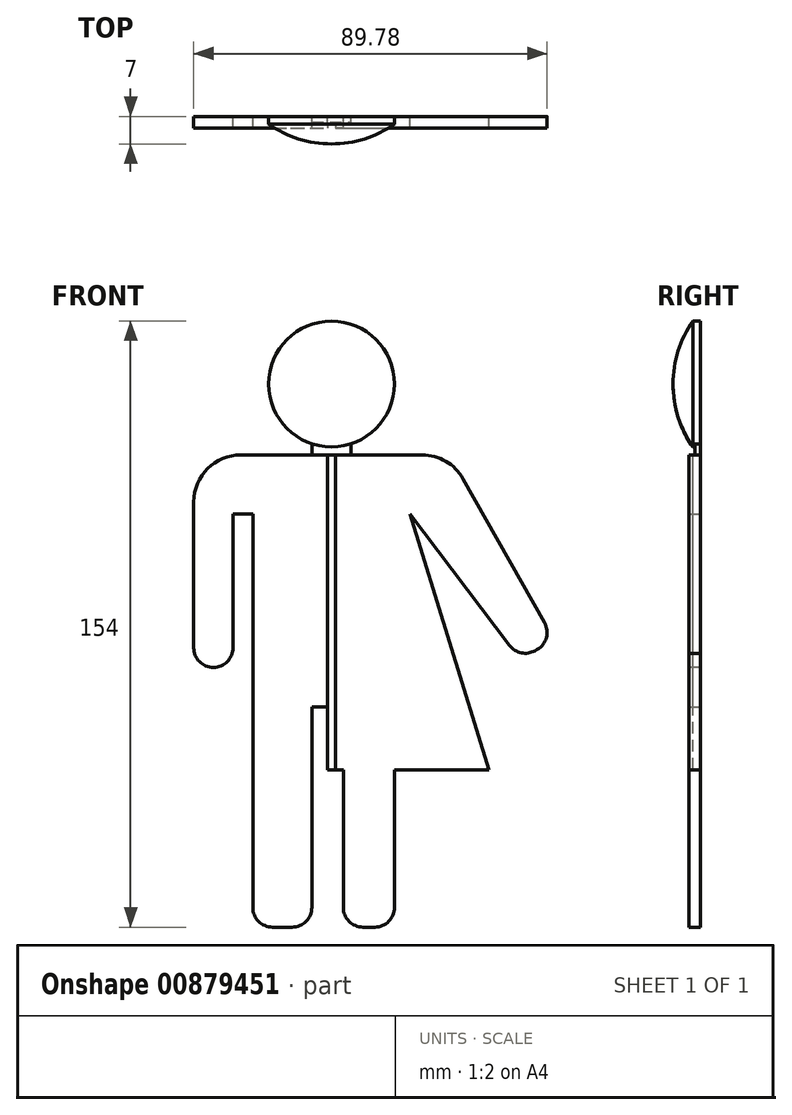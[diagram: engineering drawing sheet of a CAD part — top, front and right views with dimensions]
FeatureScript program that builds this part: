
annotation { "Feature Type Name" : "Feature", "Feature Type Description" : "" }
export const myFeature = defineFeature(function(context is Context, id is Id, definition is map)
    precondition{}
    {
        {
            var Q0;
            Q0=qCreatedBy(makeId("Front.planeOp"),FACE);
            var sketch = newSketch(context, id + "F0", { "sketchPlane" : qUnion([Q0])});
            skLineSegment(sketch, "E0.bottom", {"start": v(-60, 100) * mm, "end": v(60, 100) * mm});
            skLineSegment(sketch, "E0.top", {"start": v(-60, -100) * mm, "end": v(60, -100) * mm});
            skLineSegment(sketch, "E0.left", {"start": v(-60, 100) * mm, "end": v(-60, -100) * mm});
            skLineSegment(sketch, "E0.right", {"start": v(60, 100) * mm, "end": v(60, -100) * mm});
            skPoint(sketch, "E0.middle", {"position": v(0, 0) * mm});
            skCircle(sketch, "E1", {"center": v(0, 65) * mm, "radius": 15 * mm});
            skLineSegment(sketch, "E2.bottom", {"start": v(-20, 47) * mm, "end": v(20, 47) * mm});
            skLineSegment(sketch, "E2.top", {"start": v(-20, -73) * mm, "end": v(20, -73) * mm});
            skLineSegment(sketch, "E2.left", {"start": v(-20, 47) * mm, "end": v(-20, -73) * mm});
            skLineSegment(sketch, "E2.right", {"start": v(20, 47) * mm, "end": v(20, -73) * mm});
            skLineSegment(sketch, "E3.bottom", {"start": v(-20, 47) * mm, "end": v(-35, 47) * mm});
            skLineSegment(sketch, "E3.top", {"start": v(-20, -7) * mm, "end": v(-35, -7) * mm});
            skLineSegment(sketch, "E3.left", {"start": v(-20, 47) * mm, "end": v(-20, -7) * mm});
            skLineSegment(sketch, "E3.right", {"start": v(-35, 47) * mm, "end": v(-35, -7) * mm});
            skLineSegment(sketch, "E4.bottom", {"start": v(-5, -73) * mm, "end": v(3, -73) * mm});
            skLineSegment(sketch, "E4.top", {"start": v(-5, -17) * mm, "end": v(3, -17) * mm});
            skLineSegment(sketch, "E4.left", {"start": v(-5, -73) * mm, "end": v(-5, -17) * mm});
            skLineSegment(sketch, "E4.right", {"start": v(3, -73) * mm, "end": v(3, -17) * mm});
            skLineSegment(sketch, "E5.bottom", {"start": v(20, -73) * mm, "end": v(16, -73) * mm});
            skLineSegment(sketch, "E5.top", {"start": v(20, -33) * mm, "end": v(16, -33) * mm});
            skLineSegment(sketch, "E5.left", {"start": v(20, -73) * mm, "end": v(20, -33) * mm});
            skLineSegment(sketch, "E5.right", {"start": v(16, -73) * mm, "end": v(16, -33) * mm});
            skLineSegment(sketch, "E6", {"start": v(20, -33) * mm, "end": v(40, -33) * mm});
            skLineSegment(sketch, "E7", {"start": v(40, -33) * mm, "end": v(20, 32) * mm});
            skLineSegment(sketch, "E8", {"start": v(20, 47) * mm, "end": v(30, 47) * mm});
            skLineSegment(sketch, "E9", {"start": v(30, 47) * mm, "end": v(56.59, 0) * mm});
            skLineSegment(sketch, "E10", {"start": v(56.59, 0) * mm, "end": v(47.89, -4.92) * mm});
            skLineSegment(sketch, "E11", {"start": v(47.89, -4.92) * mm, "end": v(20, 32) * mm});
            skLineSegment(sketch, "E12.bottom", {"start": v(-20, -7) * mm, "end": v(-25, -7) * mm});
            skLineSegment(sketch, "E12.top", {"start": v(-20, 32) * mm, "end": v(-25, 32) * mm});
            skLineSegment(sketch, "E12.left", {"start": v(-20, -7) * mm, "end": v(-20, 32) * mm});
            skLineSegment(sketch, "E12.right", {"start": v(-25, -7) * mm, "end": v(-25, 32) * mm});
            skLineSegment(sketch, "E13.bottom", {"start": v(-5, 53) * mm, "end": v(5, 53) * mm});
            skLineSegment(sketch, "E13.top", {"start": v(-5, 41) * mm, "end": v(5, 41) * mm});
            skLineSegment(sketch, "E13.left", {"start": v(-5, 53) * mm, "end": v(-5, 41) * mm});
            skLineSegment(sketch, "E13.right", {"start": v(5, 53) * mm, "end": v(5, 41) * mm});
            skPoint(sketch, "E13.middle", {"position": v(0, 47) * mm});
            skLineSegment(sketch, "E14.bottom", {"start": v(16, -33) * mm, "end": v(-1, -33) * mm});
            skLineSegment(sketch, "E14.top", {"start": v(16, -17) * mm, "end": v(-1, -17) * mm});
            skLineSegment(sketch, "E14.left", {"start": v(16, -33) * mm, "end": v(16, -17) * mm});
            skLineSegment(sketch, "E14.right", {"start": v(-1, -33) * mm, "end": v(-1, -17) * mm});
            skSolve(sketch);
        }
        {
            var Q0;
            {var subQ5=sQuery(id+"F0.wireOp",EDGE,"E13.top");Q0=makeQuery(id+"F0.imprint","IMPRINT",FACE,{"disambiguationData":[TD([[makeQuery(id+"F0.imprint","IMPRINT",EDGE,{"derivedFrom":subQ5}),1.0]])]});}
            var Q1;
            {var subQ6=sQuery(id+"F0.wireOp",EDGE,"E2.left");Q1=makeQuery(id+"F0.imprint","IMPRINT",FACE,{"disambiguationData":[TD([[makeQuery(id+"F0.imprint","IMPRINT",EDGE,{"derivedFrom":subQ6}),1.0]])]});}
            var Q2;
            Q2=makeQuery(id+"F0.imprint","IMPRINT",FACE,{"disambiguationData":[TD([[makeQuery(id+"F0.imprint","IMPRINT",EDGE,{"derivedFrom":sQuery(id+"F0.wireOp",EDGE,"E3.bottom")}),1.0]])]});
            var Q3;
            {var subQ0=sQuery(id+"F0.wireOp",EDGE,"E6");Q3=makeQuery(id+"F0.imprint","IMPRINT",FACE,{"disambiguationData":[TD([[makeQuery(id+"F0.imprint","IMPRINT",EDGE,{"derivedFrom":subQ0}),1.0]])]});}
            var Q4;
            {var subQ0=sQuery(id+"F0.wireOp",EDGE,"E8");Q4=makeQuery(id+"F0.imprint","IMPRINT",FACE,{"disambiguationData":[TD([[makeQuery(id+"F0.imprint","IMPRINT",EDGE,{"derivedFrom":subQ0}),-1.0]])]});}
            var Q5;
            {var subQ5=sQuery(id+"F0.wireOp",EDGE,"E14.left");Q5=makeQuery(id+"F0.imprint","IMPRINT",FACE,{"disambiguationData":[TD([[makeQuery(id+"F0.imprint","IMPRINT",EDGE,{"derivedFrom":subQ5}),1.0]])]});}
            var Q6;
            {var subQ5=sQuery(id+"F0.wireOp",EDGE,"E14.right");Q6=makeQuery(id+"F0.imprint","IMPRINT",FACE,{"disambiguationData":[TD([[makeQuery(id+"F0.imprint","IMPRINT",EDGE,{"derivedFrom":subQ5}),-1.0]])]});}
            var Q7;
            {var subQ0=sQuery(id+"F0.wireOp",EDGE,"E5.right");Q7=makeQuery(id+"F0.imprint","IMPRINT",FACE,{"disambiguationData":[TD([[makeQuery(id+"F0.imprint","IMPRINT",EDGE,{"derivedFrom":subQ0}),1.0]])]});}
            extrude(context, id + "F1", {"entities" : qUnion([Q0, Q1, Q2, Q3, Q4, Q5, Q6, Q7]), "depth" : 3 * mm, "offsetDistance" : 25 * mm});
        }
        {
            var Q0;
            Q0=makeQuery(id+"F1.opExtrude","SWEPT_EDGE",EDGE,{"disambiguationData":[OSD([sQuery(id+"F0.wireOp",EDGE,"E9"),sQuery(id+"F0.wireOp",EDGE,"E10")])]});
            var Q1;
            Q1=makeQuery(id+"F1.opExtrude","SWEPT_EDGE",EDGE,{"disambiguationData":[OSD([sQuery(id+"F0.wireOp",EDGE,"E10"),sQuery(id+"F0.wireOp",EDGE,"E11")])]});
            var Q2;
            Q2=makeQuery(id+"F1.opExtrude","SWEPT_EDGE",EDGE,{"disambiguationData":[OSD([sQuery(id+"F0.wireOp",EDGE,"E3.top"),sQuery(id+"F0.wireOp",EDGE,"E12.bottom"),sQuery(id+"F0.wireOp",EDGE,"E12.right")])]});
            var Q3;
            Q3=makeQuery(id+"F1.opExtrude","SWEPT_EDGE",EDGE,{"disambiguationData":[OSD([sQuery(id+"F0.wireOp",EDGE,"E3.top"),sQuery(id+"F0.wireOp",EDGE,"E3.right")])]});
            var Q4;
            Q4=makeQuery(id+"F1.opExtrude","SWEPT_EDGE",EDGE,{"disambiguationData":[OSD([sQuery(id+"F0.wireOp",EDGE,"E2.top"),sQuery(id+"F0.wireOp",EDGE,"E5.bottom"),sQuery(id+"F0.wireOp",EDGE,"E5.right")])]});
            var Q5;
            Q5=makeQuery(id+"F1.opExtrude","SWEPT_EDGE",EDGE,{"disambiguationData":[OSD([sQuery(id+"F0.wireOp",EDGE,"E2.top"),sQuery(id+"F0.wireOp",EDGE,"E4.bottom"),sQuery(id+"F0.wireOp",EDGE,"E4.right")])]});
            var Q6;
            Q6=makeQuery(id+"F1.opExtrude","SWEPT_EDGE",EDGE,{"disambiguationData":[OSD([sQuery(id+"F0.wireOp",EDGE,"E2.top"),sQuery(id+"F0.wireOp",EDGE,"E2.left")])]});
            var Q7;
            Q7=makeQuery(id+"F1.opExtrude","SWEPT_EDGE",EDGE,{"disambiguationData":[OSD([sQuery(id+"F0.wireOp",EDGE,"E2.top"),sQuery(id+"F0.wireOp",EDGE,"E4.bottom"),sQuery(id+"F0.wireOp",EDGE,"E4.left")])]});
            fillet(context, id + "F2", {"entities" : qUnion([Q0, Q1, Q2, Q3, Q4, Q5, Q6, Q7]), "radius" : 5 * mm, "tangentPropagation" : true, "allowEdgeOverflow" : false});
        }
        {
            var Q0;
            {var subQ0=sQuery(id+"F0.wireOp",EDGE,"E13.left");var subQ1=sQuery(id+"F0.wireOp",EDGE,"E1");var subQ2=makeQuery(id+"F0.imprint","INTERSECT",VERTEX,{"derivedFrom":[subQ1,subQ0]});Q0=makeQuery(id+"F0.imprint","IMPRINT",FACE,{"disambiguationData":[TD([[makeQuery(id+"F0.imprint","IMPRINT",EDGE,{"disambiguationData":[TD([[subQ2,-1.0]])],"derivedFrom":subQ1}),-1.0]])]});}
            extrude(context, id + "F3", {"entities" : qUnion([Q0]), "depth" : 1.5 * mm, "offsetDistance" : 25 * mm});
        }
        {
            var Q0;
            Q0=makeQuery(id+"F1.opExtrude","SWEPT_EDGE",EDGE,{"disambiguationData":[OSD([sQuery(id+"F0.wireOp",EDGE,"E8"),sQuery(id+"F0.wireOp",EDGE,"E9")])]});
            var Q1;
            Q1=makeQuery(id+"F1.opExtrude","SWEPT_EDGE",EDGE,{"disambiguationData":[OSD([sQuery(id+"F0.wireOp",EDGE,"E3.bottom"),sQuery(id+"F0.wireOp",EDGE,"E3.right")])]});
            fillet(context, id + "F4", {"entities" : qUnion([Q0, Q1]), "radius" : 12 * mm, "tangentPropagation" : true, "allowEdgeOverflow" : false});
        }
        {
            var Q0;
            Q0=qCreatedBy(makeId("Right.planeOp"),FACE);
            var sketch = newSketch(context, id + "F5", { "sketchPlane" : qUnion([Q0])});
            skLineSegment(sketch, "E15", {"start": v(0, 65) * mm, "end": v(-7, 65) * mm});
            skLineSegment(sketch, "E16", {"start": v(0, 65) * mm, "end": v(0, 49) * mm});
            skLineSegment(sketch, "E17", {"start": v(0, 49) * mm, "end": v(-2, 49) * mm});
            skArc(sketch, "E18", {"start": v(-7, 65) * mm, "mid": v(-5.72, 56.62) * mm, "end": v(-2, 49) * mm});
            skSolve(sketch);
        }
        {
            var Q0;
            Q0=makeQuery(id+"F5.imprint","IMPRINT",FACE,{"disambiguationData":[TD([[makeQuery(id+"F5.imprint","IMPRINT",EDGE,{"derivedFrom":sQuery(id+"F5.wireOp",EDGE,"E15")}),1.0]])]});
            var Q1;
            Q1=sQuery(id+"F5.wireOp",EDGE,"E15");
            revolve(context, id + "F6", {"operationType" : NewBodyOperationType.ADD, "surfaceOperationType" : NewSurfaceOperationType.NEW, "entities" : qUnion([Q0]), "axis" : qUnion([Q1]), "revolveType" : RevolveType.FULL});
        }
        {
            var Q0;
            Q0=makeQuery(id+"F1.opExtrude","CAP_FACE",FACE,{"disambiguationData":[OSD([sQuery(id+"F0.wireOp",EDGE,"E2.bottom"),sQuery(id+"F0.wireOp",EDGE,"E2.top"),sQuery(id+"F0.wireOp",EDGE,"E2.left"),sQuery(id+"F0.wireOp",EDGE,"E3.bottom"),sQuery(id+"F0.wireOp",EDGE,"E3.top"),sQuery(id+"F0.wireOp",EDGE,"E3.right"),sQuery(id+"F0.wireOp",EDGE,"E4.top"),sQuery(id+"F0.wireOp",EDGE,"E4.left"),sQuery(id+"F0.wireOp",EDGE,"E4.right"),sQuery(id+"F0.wireOp",EDGE,"E5.top"),sQuery(id+"F0.wireOp",EDGE,"E5.right"),sQuery(id+"F0.wireOp",EDGE,"E6"),sQuery(id+"F0.wireOp",EDGE,"E7"),sQuery(id+"F0.wireOp",EDGE,"E8"),sQuery(id+"F0.wireOp",EDGE,"E9"),sQuery(id+"F0.wireOp",EDGE,"E10"),sQuery(id+"F0.wireOp",EDGE,"E11"),sQuery(id+"F0.wireOp",EDGE,"E12.top"),sQuery(id+"F0.wireOp",EDGE,"E12.left"),sQuery(id+"F0.wireOp",EDGE,"E12.right"),sQuery(id+"F0.wireOp",EDGE,"E14.bottom"),sQuery(id+"F0.wireOp",EDGE,"E14.right")])],"isStart":false});
            var sketch = newSketch(context, id + "F7", { "sketchPlane" : qUnion([Q0])});
            skLineSegment(sketch, "E19.bottom", {"start": v(-1, -33) * mm, "end": v(1, -33) * mm});
            skLineSegment(sketch, "E19.top", {"start": v(-1, 47) * mm, "end": v(1, 47) * mm});
            skLineSegment(sketch, "E19.left", {"start": v(-1, -33) * mm, "end": v(-1, 47) * mm});
            skLineSegment(sketch, "E19.right", {"start": v(1, -33) * mm, "end": v(1, 47) * mm});
            skSolve(sketch);
        }
        {
            var Q0;
            {var subQ2=sQuery(id+"F7.wireOp",EDGE,"E19.bottom");Q0=makeQuery(id+"F7.imprint","IMPRINT",FACE,{"disambiguationData":[TD([[makeQuery(id+"F7.imprint","IMPRINT",EDGE,{"derivedFrom":subQ2}),-1.0]])]});}
            extrude(context, id + "F8", {"entities" : qUnion([Q0]), "operationType" : NewBodyOperationType.REMOVE, "oppositeDirection" : true, "depth" : 1 * mm, "offsetDistance" : 25 * mm});
        }
    });
